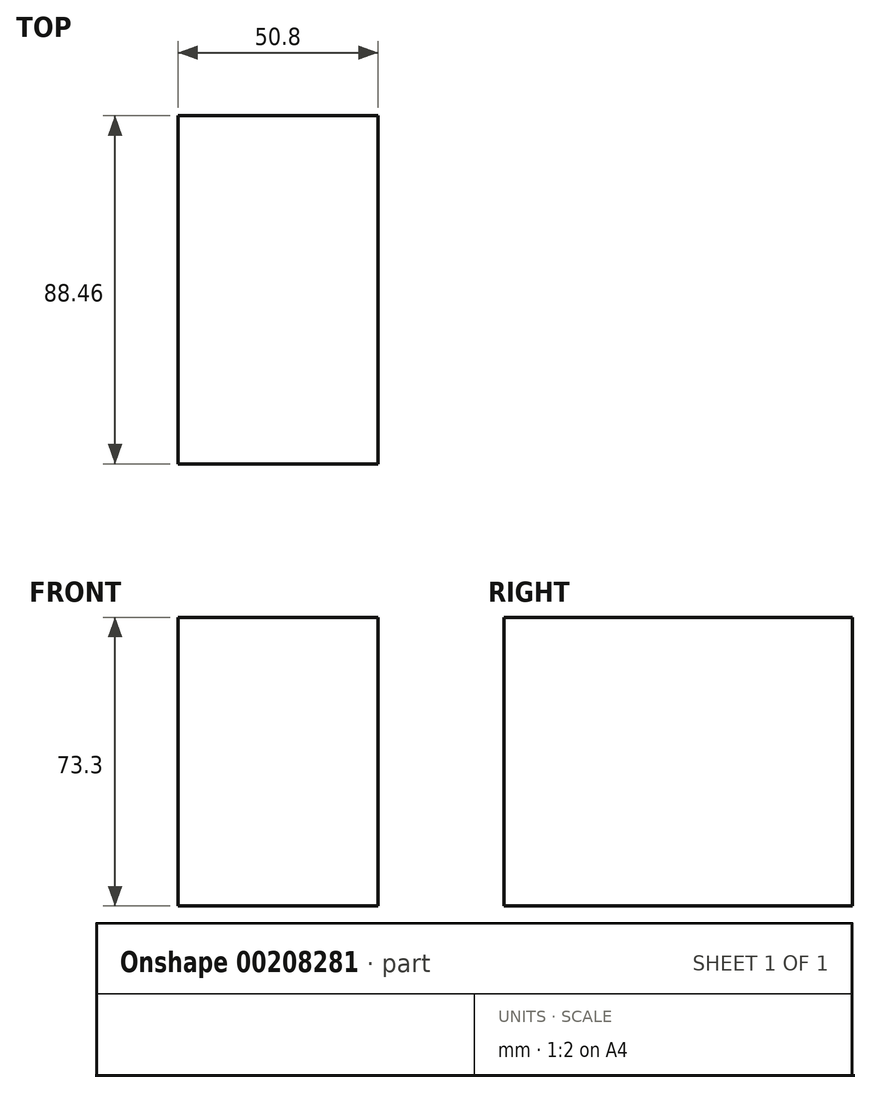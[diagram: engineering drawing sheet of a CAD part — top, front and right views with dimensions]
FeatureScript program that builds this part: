
annotation { "Feature Type Name" : "Feature", "Feature Type Description" : "" }
export const myFeature = defineFeature(function(context is Context, id is Id, definition is map)
    precondition{}
    {
        {
            var Q0;
            Q0=qCreatedBy(makeId("Right.planeOp"),FACE);
            var sketch = newSketch(context, id + "F0", { "sketchPlane" : qUnion([Q0])});
            skLineSegment(sketch, "E0.bottom", {"start": v(-42.51, 0) * mm, "end": v(45.95, 0) * mm});
            skLineSegment(sketch, "E0.top", {"start": v(-42.51, -73.3) * mm, "end": v(45.95, -73.3) * mm});
            skLineSegment(sketch, "E0.left", {"start": v(-42.51, 0) * mm, "end": v(-42.51, -73.3) * mm});
            skLineSegment(sketch, "E0.right", {"start": v(45.95, 0) * mm, "end": v(45.95, -73.3) * mm});
            skLineSegment(sketch, "E1", {"start": v(0, 60.8) * mm, "end": v(43.76, 42.04) * mm});
            skLineSegment(sketch, "E2", {"start": v(43.76, 42.04) * mm, "end": v(45.95, 0) * mm});
            skLineSegment(sketch, "E3.MirrorCS", {"start": v(0, 60.8) * mm, "end": v(-43.76, 42.04) * mm});
            skLineSegment(sketch, "E4.MirrorCS", {"start": v(-43.76, 42.04) * mm, "end": v(-45.95, 0) * mm});
            skSolve(sketch);
        }
        {
            var Q0;
            Q0=makeQuery(id+"F0.imprint","IMPRINT",FACE,{"disambiguationData":[TD([[makeQuery(id+"F0.imprint","IMPRINT",EDGE,{"derivedFrom":sQuery(id+"F0.wireOp",EDGE,"E0.bottom")}),-1.0]])]});
            extrude(context, id + "F1", {"entities" : qUnion([Q0]), "depth" : 25.4 * mm});
        }
        {
            var Q0;
            Q0=makeQuery(id+"F1.opExtrude","CAP_FACE",FACE,{"disambiguationData":[OSD([sQuery(id+"F0.wireOp",EDGE,"E0.bottom"),sQuery(id+"F0.wireOp",EDGE,"E0.top"),sQuery(id+"F0.wireOp",EDGE,"E0.left"),sQuery(id+"F0.wireOp",EDGE,"E0.right")])],"isStart":false});
            extrude(context, id + "F2", {"entities" : qUnion([Q0]), "operationType" : NewBodyOperationType.ADD, "depth" : 25.4 * mm});
        }
        {
            var Q0;
            Q0 = qSketchRegion(id + "F0", true);
            extrude(context, id + "F3", {"entities" : qUnion([Q0]), "operationType" : NewBodyOperationType.ADD, "depth" : 25.4 * mm});
        }
    });
